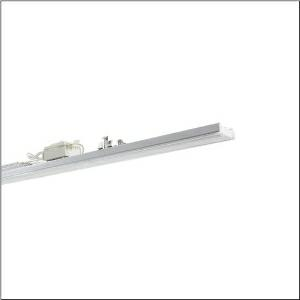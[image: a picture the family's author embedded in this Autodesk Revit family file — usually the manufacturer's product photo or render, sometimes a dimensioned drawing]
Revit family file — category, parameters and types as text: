
# Revit family: licross_r__21_recessed_mo_52tl14mn4axg_742d
name_source: partatom
category: Lighting Fixtures
units: mm (PartAtom-declared; Revit-internal decimal feet)

## family parameters
Cut with Voids When Loaded = No
Host = Face
Light Source = No
Part Type = Normal
Room Calculation Point = No
Round Connector Dimension = Use Diameter
Shared = No

## types (1)
- --- (1 x LED, 10120 lm, 60.5 W, 4000K)
    Apparent Load = 61 VA
    CIE Flux Codes = 56 84 97 100 100
    Color Rendering = 80
    Color Temperature = 4000K
    Default Elevation = 1800 mm
    Description = Licross® 21 Recessed MO, luminaire insert, of sheet steel, galvanised, coil coated, white, length: 1.500mm, width: 66mm, height: 67mm, LED rated luminous flux: 10.120lm, light colour: 840, control gear: ON/OFF Multilumen, with plug, 3-pole, with phase selection, mains connection: 220..240V, AC, 50/60Hz, rated input power: 61W, halogen-free wiring, primary light control with lens, of plastic, primary optical cover: cover, of PMMA, light emission: direct distribution, primary light characteristic: asymmetric, protection rating (complete): IP40, insulation class (complete): insulation class I (protective earthing), certification: CE, ENEC, VDE, UKCA, protection symbol: D if used in an environment without relevant dust loads with corresponding accessories, impact resistance: IK06, permissible ambient temperature for indoor applications: -35..+40°C, corresponds to IFS (International Featured Standards) requirements for safety and quality in the food industry, reducing of maximum allowable ambient temperature of 5°C with ceiling mounting, LABS conformity tested according to VDMA 24364:2018-05, packaging unit: 1 piece
    Height = 58 mm
    Lamp = 1 x LED
    Lamp Light Flux = 10120 lm
    Lamp Power = 60.5 W
    Lamp count = 1
    Length = 1500 mm
    Luminous efficacy = 167 lm/W
    Manufacturer = Siteco
    ModVariant = No
    Model = 52TL14MN4AXG
    Mounting Place = Ceiling
    Mounting Type = Pendant
    Number of Poles = 1
    OnlyDefault = Yes
    Power Factor = 1
    Product Name = Licross® 21 Recessed MO
    Product group = luminaire insert
    ProductGroupID = 902
    Protection Class = Protection class I
    Protection Degree = IP 40
    RLX_Detail_Level = 1
    RLX_Emergency_Light_Flux = 0 lm
    RLX_Emergency_Type = 0
    RLX_Emergency_Type_DB = No
    RlxData = <blob elided: 22741 chars, md5=d2cddc6a>
    Socket = socket
    Standby Power = 0 W
    System Light Flux = 10120 lm
    System Power = 61 W
    Type Comments = factory setting: luminous flux: 100 % | (A | C | E) | 140 mA
    Type Image = l_1296930.jpg
    URL = http://relux.com
    VarID = @adj_108098
    Voltage = 0 V
    Weight = 0.00 kg
    Width = 66 mm

## geometry (parser evidence)
native form markers: Blend x4, Sweep x11
no freeform markers — native parametric forms only
